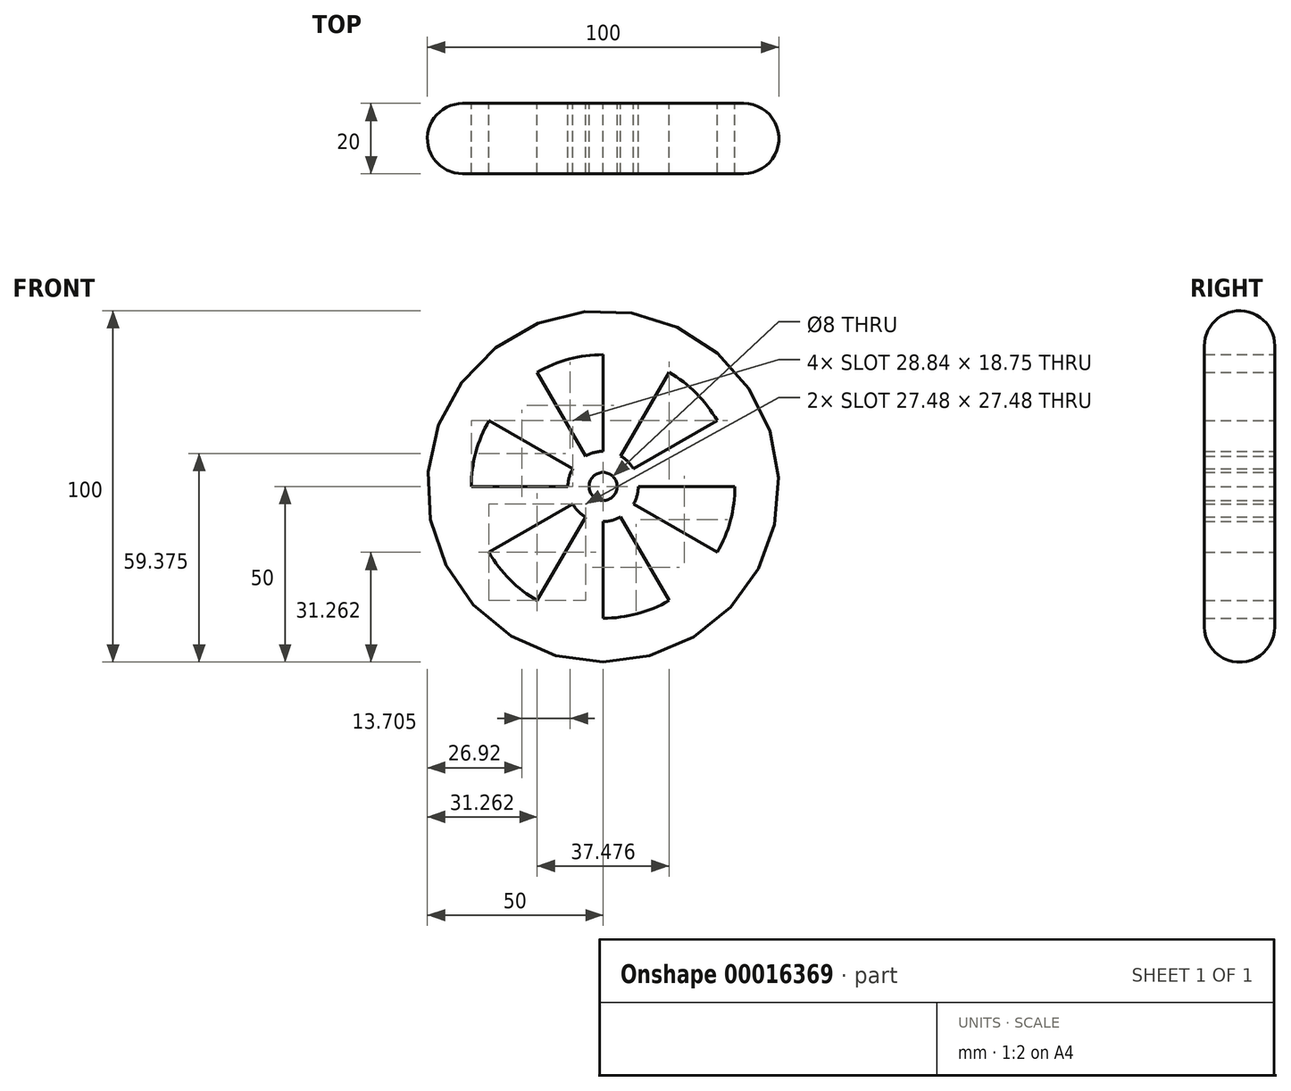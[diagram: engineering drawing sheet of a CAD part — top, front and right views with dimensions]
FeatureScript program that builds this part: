
annotation { "Feature Type Name" : "Feature", "Feature Type Description" : "" }
export const myFeature = defineFeature(function(context is Context, id is Id, definition is map)
    precondition{}
    {
        {
            var Q0;
            Q0=qCreatedBy(makeId("Front.planeOp"),FACE);
            var sketch = newSketch(context, id + "F0", { "sketchPlane" : qUnion([Q0])});
            skCircle(sketch, "E0", {"center": v(0, 0) * mm, "radius": 50 * mm});
            skCircle(sketch, "E1", {"center": v(0, 0) * mm, "radius": 4 * mm});
            skCircle(sketch, "E2", {"center": v(0, 0) * mm, "radius": 10 * mm});
            skCircle(sketch, "E3", {"center": v(0, 0) * mm, "radius": 37.5 * mm});
            skLineSegment(sketch, "E4", {"start": v(0, 10) * mm, "end": v(0, 37.5) * mm});
            skLineSegment(sketch, "E5", {"start": v(0, 10) * mm, "end": v(0, 0) * mm, "construction": true});
            skLineSegment(sketch, "E6.1.0", {"start": v(-5, 8.66) * mm, "end": v(-18.75, 32.48) * mm});
            skLineSegment(sketch, "E6.2.0", {"start": v(-8.66, 5) * mm, "end": v(-32.48, 18.75) * mm});
            skLineSegment(sketch, "E6.3.0", {"start": v(-10, 0) * mm, "end": v(-37.5, 0) * mm});
            skLineSegment(sketch, "E6.4.0", {"start": v(-8.66, -5) * mm, "end": v(-32.48, -18.75) * mm});
            skLineSegment(sketch, "E6.5.0", {"start": v(-5, -8.66) * mm, "end": v(-18.75, -32.48) * mm});
            skLineSegment(sketch, "E6.6.0", {"start": v(0, -10) * mm, "end": v(0, -37.5) * mm});
            skLineSegment(sketch, "E6.7.0", {"start": v(5, -8.66) * mm, "end": v(18.75, -32.48) * mm});
            skLineSegment(sketch, "E6.8.0", {"start": v(8.66, -5) * mm, "end": v(32.48, -18.75) * mm});
            skLineSegment(sketch, "E6.9.0", {"start": v(10, 0) * mm, "end": v(37.5, 0) * mm});
            skLineSegment(sketch, "E6.10.0", {"start": v(8.66, 5) * mm, "end": v(32.48, 18.75) * mm});
            skLineSegment(sketch, "E6.11.0", {"start": v(5, 8.66) * mm, "end": v(18.75, 32.48) * mm});
            skSolve(sketch);
        }
        {
            var Q0;
            Q0=makeQuery(id+"F0.imprint","IMPRINT",FACE,{"disambiguationData":[TD([[makeQuery(id+"F0.imprint","IMPRINT",EDGE,{"derivedFrom":sQuery(id+"F0.wireOp",EDGE,"E0")}),1.0]])]});
            var Q1;
            {var subQ1=sQuery(id+"F0.wireOp",EDGE,"E6.1.0");Q1=makeQuery(id+"F0.imprint","IMPRINT",FACE,{"disambiguationData":[TD([[makeQuery(id+"F0.imprint","IMPRINT",EDGE,{"derivedFrom":subQ1}),1.0]])]});}
            var Q2;
            {var subQ1=sQuery(id+"F0.wireOp",EDGE,"E4");Q2=makeQuery(id+"F0.imprint","IMPRINT",FACE,{"disambiguationData":[TD([[makeQuery(id+"F0.imprint","IMPRINT",EDGE,{"derivedFrom":subQ1}),-1.0]])]});}
            var Q3;
            {var subQ1=sQuery(id+"F0.wireOp",EDGE,"E6.9.0");Q3=makeQuery(id+"F0.imprint","IMPRINT",FACE,{"disambiguationData":[TD([[makeQuery(id+"F0.imprint","IMPRINT",EDGE,{"derivedFrom":subQ1}),1.0]])]});}
            var Q4;
            {var subQ1=sQuery(id+"F0.wireOp",EDGE,"E6.7.0");Q4=makeQuery(id+"F0.imprint","IMPRINT",FACE,{"disambiguationData":[TD([[makeQuery(id+"F0.imprint","IMPRINT",EDGE,{"derivedFrom":subQ1}),1.0]])]});}
            var Q5;
            {var subQ1=sQuery(id+"F0.wireOp",EDGE,"E6.5.0");Q5=makeQuery(id+"F0.imprint","IMPRINT",FACE,{"disambiguationData":[TD([[makeQuery(id+"F0.imprint","IMPRINT",EDGE,{"derivedFrom":subQ1}),1.0]])]});}
            var Q6;
            {var subQ1=sQuery(id+"F0.wireOp",EDGE,"E6.3.0");Q6=makeQuery(id+"F0.imprint","IMPRINT",FACE,{"disambiguationData":[TD([[makeQuery(id+"F0.imprint","IMPRINT",EDGE,{"derivedFrom":subQ1}),1.0]])]});}
            var Q7;
            Q7=makeQuery(id+"F0.imprint","IMPRINT",FACE,{"disambiguationData":[TD([[makeQuery(id+"F0.imprint","IMPRINT",EDGE,{"derivedFrom":sQuery(id+"F0.wireOp",EDGE,"E1")}),-1.0]])]});
            extrude(context, id + "F1", {"entities" : qUnion([Q0, Q1, Q2, Q3, Q4, Q5, Q6, Q7]), "depth" : 20 * mm});
        }
        {
            var Q0;
            Q0=makeQuery(id+"F1.opExtrude","CAP_EDGE",EDGE,{"disambiguationData":[OSD([sQuery(id+"F0.wireOp",EDGE,"E0")])],"isStart":false});
            var Q1;
            Q1=makeQuery(id+"F1.opExtrude","CAP_EDGE",EDGE,{"disambiguationData":[OSD([sQuery(id+"F0.wireOp",EDGE,"E0")])],"isStart":true});
            fillet(context, id + "F2", {"entities" : qUnion([Q0, Q1]), "radius" : 10 * mm, "tangentPropagation" : true, "allowEdgeOverflow" : false});
        }
    });
